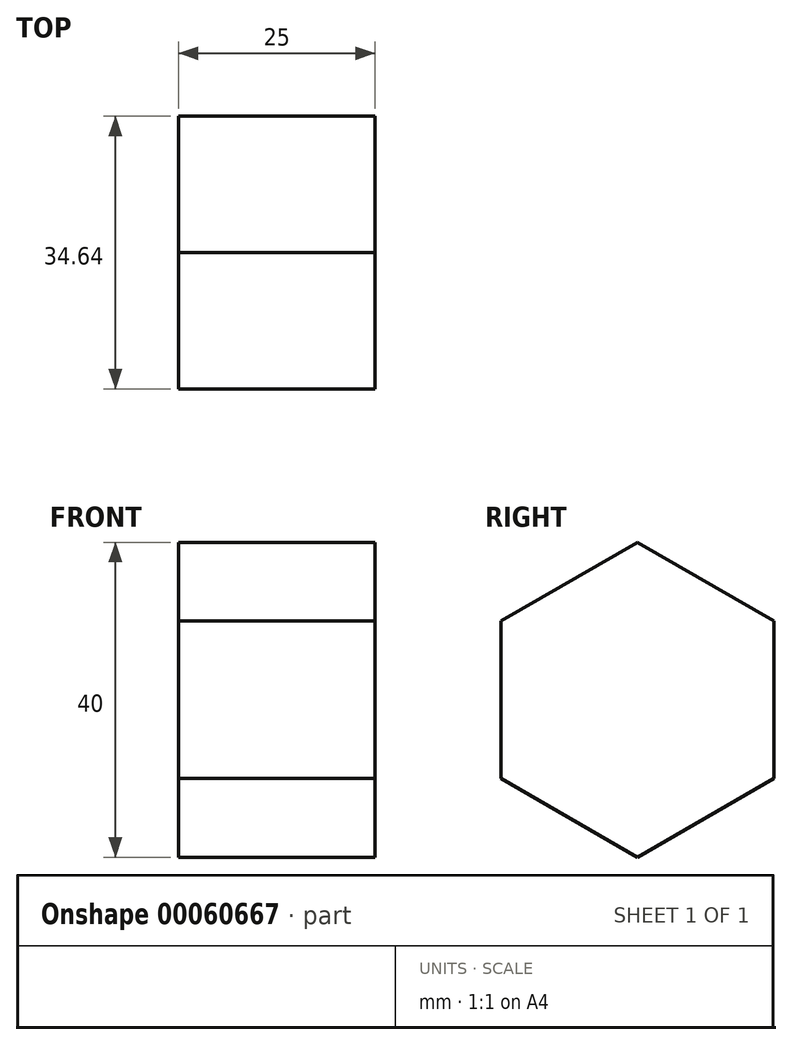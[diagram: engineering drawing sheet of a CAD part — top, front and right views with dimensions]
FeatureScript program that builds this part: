
annotation { "Feature Type Name" : "Feature", "Feature Type Description" : "" }
export const myFeature = defineFeature(function(context is Context, id is Id, definition is map)
    precondition{}
    {
        {
            var Q0;
            Q0=qCreatedBy(makeId("Front.planeOp"),FACE);
            var sketch = newSketch(context, id + "F0", { "sketchPlane" : qUnion([Q0])});
            skLineSegment(sketch, "E0", {"start": v(0, 0) * mm, "end": v(0, 75) * mm});
            skLineSegment(sketch, "E1", {"start": v(0, 75) * mm, "end": v(50, 75) * mm});
            skLineSegment(sketch, "E2", {"start": v(50, 75) * mm, "end": v(64.43, 50) * mm});
            skLineSegment(sketch, "E3", {"start": v(64.43, 50) * mm, "end": v(95, 50) * mm});
            skLineSegment(sketch, "E4", {"start": v(100, 45) * mm, "end": v(100, 0) * mm});
            skLineSegment(sketch, "E5", {"start": v(100, 0) * mm, "end": v(0, 0) * mm});
            skPoint(sketch, "E6.visualSharp", {"position": v(100, 50) * mm});
            skArc(sketch, "E6.filletArc", {"start": v(100, 45) * mm, "mid": v(98.54, 48.54) * mm, "end": v(95, 50) * mm});
            skSolve(sketch);
        }
        {
            var Q0;
            Q0=sQuery(id+"F0.wireOp",EDGE,"E1");
            var Q1;
            Q1=sQuery(id+"F0.wireOp",EDGE,"E2");
            var Q2;
            Q2=sQuery(id+"F0.wireOp",EDGE,"E3");
            var Q3;
            Q3=sQuery(id+"F0.wireOp",EDGE,"E6.filletArc");
            var Q4;
            Q4=sQuery(id+"F0.wireOp",EDGE,"E0");
            var Q5;
            Q5=sQuery(id+"F0.wireOp",EDGE,"E4");
            var Q6;
            Q6=sQuery(id+"F0.wireOp",EDGE,"E5");
            revolve(context, id + "F1", {"bodyType" : ToolBodyType.SURFACE, "surfaceEntities" : qUnion([Q0, Q1, Q2, Q3, Q4, Q5]), "axis" : qUnion([Q6]), "revolveType" : RevolveType.FULL});
        }
        {
            var Q0;
            Q0=makeQuery(id+"F1.opRevolve","SWEPT_EDGE",EDGE,{"disambiguationData":[OSD([sQuery(id+"F0.wireOp",VERTEX,"E2.start")])]});
            chamfer(context, id + "F2", {"entities" : qUnion([Q0]), "width" : 5 * mm, "tangentPropagation" : true});
        }
        {
            var Q0;
            Q0=makeQuery(id+"F1.opRevolve","SWEPT_FACE",FACE,{"disambiguationData":[OSD([sQuery(id+"F0.wireOp",EDGE,"E4")])]});
            var sketch = newSketch(context, id + "F3", { "sketchPlane" : qUnion([Q0])});
            skCircle(sketch, "E7.cCircle", {"center": v(0, 0) * mm, "radius": 20 * mm, "construction": true});
            skLineSegment(sketch, "E7.0", {"start": v(0, 20) * mm, "end": v(17.32, 10) * mm});
            skLineSegment(sketch, "E7.1", {"start": v(17.32, 10) * mm, "end": v(17.32, -10) * mm});
            skLineSegment(sketch, "E7.2", {"start": v(17.32, -10) * mm, "end": v(0, -20) * mm});
            skLineSegment(sketch, "E7.3", {"start": v(0, -20) * mm, "end": v(-17.32, -10) * mm});
            skLineSegment(sketch, "E7.4", {"start": v(-17.32, -10) * mm, "end": v(-17.32, 10) * mm});
            skLineSegment(sketch, "E7.5", {"start": v(-17.32, 10) * mm, "end": v(0, 20) * mm});
            skSolve(sketch);
        }
        {
            var Q0;
            Q0 = qSketchRegion(id + "F3", true);
            extrude(context, id + "F4", {"entities" : qUnion([Q0]), "depth" : 25 * mm});
        }
    });
